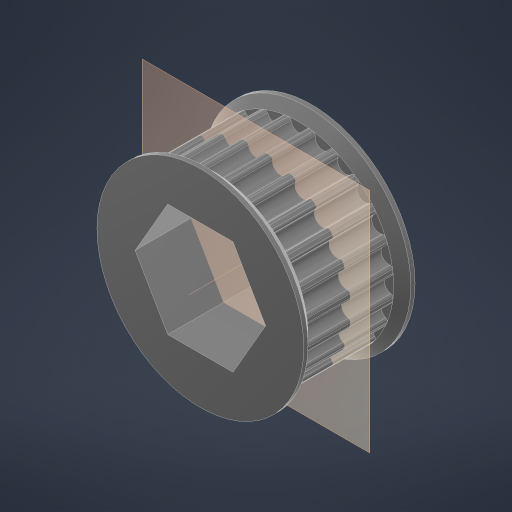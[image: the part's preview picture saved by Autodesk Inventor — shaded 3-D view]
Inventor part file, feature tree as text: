
AUTODESK INVENTOR PART (.ipt)
format: ipt  version: 2023.4 (Build 274418000, 418)  size: 388,096 bytes
history: native  units: in
note: dims shown in document units (in); Inventor stores cm internally (conversion verified against a paired STEP export)
features: extrude x6, mirror x2, chamfer x2, other x1, fillet x1, pattern_circular x1
ambient origin geometry x8: Origin, YZ Plane, XZ Plane, XY Plane, X Axis, Y Axis, Z Axis, Center Point
bodies: Solid1 (feature_tree)
feature tree (13):
  other  "Hex Bore"
  extrude  "HTD Base"  Depth=1.4588in
  extrude  "HTD Flange"  Depth=0.3937in TaperAngle=0.0deg
  mirror  "HTD Flanges"
  chamfer  "HTD Flange Chamfer"  Distance=0.0394in
  extrude  "GT2 Base"  Depth=0.0591in
  extrude  "GT2 Base Tooth"  TaperAngle=0.0deg  [1 undecoded]
  fillet  "GT2 Base Tooth pt. 2"  Radius=0.0394in
  pattern_circular  "GT2 Teeth"  Angle=45.0deg  [1 undecoded]
  extrude  "GT2 Flange"  Depth=0.52in
  mirror  "GT2 Flanges"
  chamfer  "GT2 Flange Chamfer"  [1 undecoded]
  extrude  "Circle Bore"  Depth=0.52in
note: 3 required parameter values undecoded (feature->parameter linkage not recoverable at this tier; creation-order binding heuristic only, values carry confidence <= 0.55)
